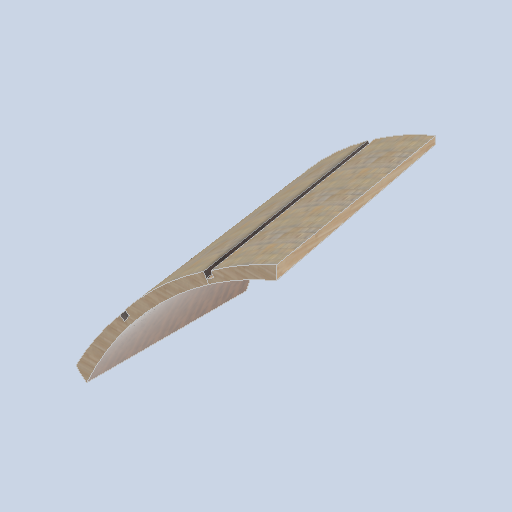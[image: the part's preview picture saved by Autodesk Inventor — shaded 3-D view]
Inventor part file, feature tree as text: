
AUTODESK INVENTOR PART (.ipt)
format: ipt  version: 2024.2 (Build 282272000, 272)  size: 264,704 bytes
history: native  units: in
note: dims shown in document units (in); Inventor stores cm internally (conversion verified against a paired STEP export)
features: sketch x7, other x3, plane x2
ambient origin geometry x8: Origin, YZ Plane, XZ Plane, XY Plane, X Axis, Y Axis, Z Axis, Center Point
bodies: Solid1 (feature_tree)
feature tree (12):
  other  "panel_block_01.ipt"
  other  "Solid1::panel_block_01.ipt"
  other  "TaggingFeature1"
  sketch  "Sketch3"  dims[d0=0.3937in]
  sketch  "Sketch8"
  sketch  "Sketch9"
  sketch  "Sketch10"
  sketch  "Sketch11"
  sketch  "Sketch14"
  sketch  "Sketch15"
  plane  "Work Plane1"
  plane  "Work Plane2"
